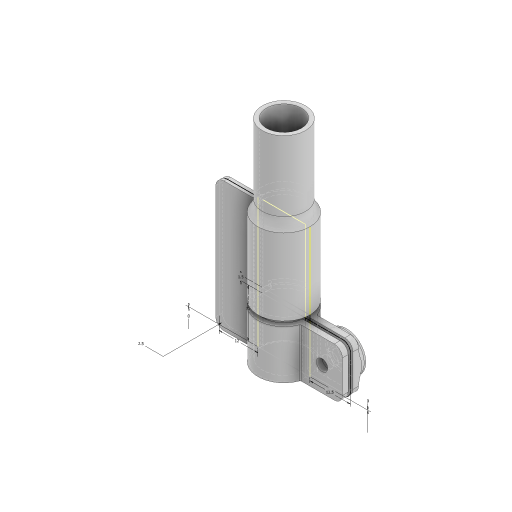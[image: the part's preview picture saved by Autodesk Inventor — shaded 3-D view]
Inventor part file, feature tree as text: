
AUTODESK INVENTOR PART (.ipt)
format: ipt  version: 2023 (Build 270158000, 158)  size: 265,728 bytes
history: native  units: mm
features: extrude x8, sketch x6, fillet x5, chamfer x1
ambient origin geometry x8: Origin, YZ Plane, XZ Plane, XY Plane, X Axis, Y Axis, Z Axis, Center Point
bodies: Solid1 (feature_tree)
feature tree (20):
  extrude  "Extrusion1"  Depth=16.0mm
  extrude  "Extrusion2"  Depth=40.0mm TaperAngle=0.0deg
  fillet  "Fillet1"  Radius=13.3mm
  fillet  "Fillet2"  Radius=10.8mm
  sketch  "Sketch3"  dims[d7=25.0mm d8=0.0mm d9=5.0mm]
  extrude  "Extrusion3"  Depth=5.0mm
  extrude  "Extrusion4"  Depth=12.0mm
  extrude  "Extrusion5"  Depth=15.0mm
  extrude  "Extrusion6"  TaperAngle=0.0deg  [1 undecoded]
  fillet  "Fillet3"  Radius=12.5mm
  fillet  "Fillet4"  Radius=2.5mm
  extrude  "Extrusion7"  Depth=0.5mm TaperAngle=0.0deg
  fillet  "Fillet5"  Radius=5.0mm
  extrude  "Extrusion8"  Depth=0.5mm
  chamfer  "Chamfer1"  Distance=0.75mm
  sketch  "Sketch1"  dims[d0=13.1mm d1=16.0mm]
  sketch  "Sketch2"  dims[d2=1.45mm d3=40.0mm d4=0.0mm d5=13.3mm d6=10.8mm]
  sketch  "Sketch4"  dims[d10=3.0mm d11=12.0mm]
  sketch  "Sketch5"  dims[d12=0.0mm d13=15.0mm]
  sketch  "Sketch6"  dims[d14=1.5mm d15=0.0mm d16=12.5mm d17=2.5mm d18=2.0mm d19=0.0mm d20=5.0mm d21=0.0mm d22=1.5mm d23=0.75mm d24=15.0mm d25=0.0mm d26=0.0mm d27=0.0mm d28=0.5mm d29=0.5mm d30=12.0mm d31=6.25mm d32=15.0mm d33=7.5mm d34=5.7mm d35=2.5mm d36=0.0mm d37=2.0mm d38=3.5mm d39=0.0mm d40=0.0mm d41=1.0mm d42=2.0mm d43=45.0deg]
note: 1 required parameter value undecoded (feature->parameter linkage not recoverable at this tier; creation-order binding heuristic only, values carry confidence <= 0.55)
